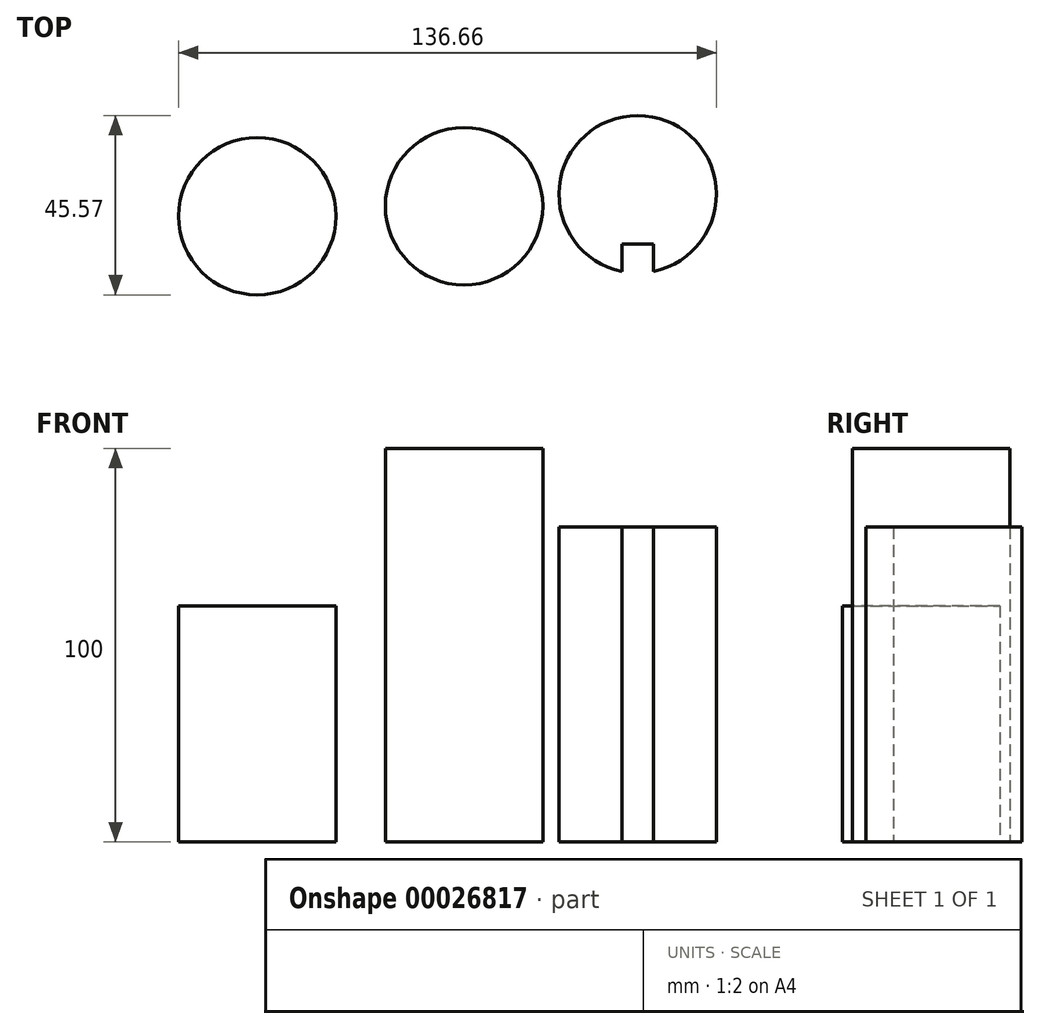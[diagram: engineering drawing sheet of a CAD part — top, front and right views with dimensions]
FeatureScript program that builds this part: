
annotation { "Feature Type Name" : "Feature", "Feature Type Description" : "" }
export const myFeature = defineFeature(function(context is Context, id is Id, definition is map)
    precondition{}
    {
        {
            var Q0;
            Q0=qCreatedBy(makeId("Top.planeOp"),FACE);
            var sketch = newSketch(context, id + "F0", { "sketchPlane" : qUnion([Q0])});
            skCircle(sketch, "E0", {"center": v(-42.04, 16.34) * mm, "radius": 20 * mm});
            skCircle(sketch, "E1", {"center": v(10.5, 18.86) * mm, "radius": 20 * mm});
            skCircle(sketch, "E2", {"center": v(54.62, 21.91) * mm, "radius": 20 * mm});
            skLineSegment(sketch, "E3", {"start": v(50.62, 2.32) * mm, "end": v(50.62, 9.32) * mm});
            skLineSegment(sketch, "E4", {"start": v(50.62, 9.32) * mm, "end": v(58.62, 9.32) * mm});
            skLineSegment(sketch, "E5", {"start": v(58.62, 9.32) * mm, "end": v(58.62, 2.32) * mm});
            skSolve(sketch);
        }
        {
            var Q0;
            Q0=makeQuery(id+"F0.imprint","IMPRINT",FACE,{"disambiguationData":[TD([[makeQuery(id+"F0.imprint","IMPRINT",EDGE,{"derivedFrom":sQuery(id+"F0.wireOp",EDGE,"E0")}),1.0]])]});
            extrude(context, id + "F1", {"entities" : qUnion([Q0]), "depth" : 60 * mm});
        }
        {
            var Q0;
            Q0=makeQuery(id+"F0.imprint","IMPRINT",FACE,{"disambiguationData":[TD([[makeQuery(id+"F0.imprint","IMPRINT",EDGE,{"derivedFrom":sQuery(id+"F0.wireOp",EDGE,"E1")}),1.0]])]});
            extrude(context, id + "F2", {"entities" : qUnion([Q0]), "depth" : 100 * mm});
        }
        {
            var Q0;
            {var subQ1=sQuery(id+"F0.wireOp",EDGE,"E3");Q0=makeQuery(id+"F0.imprint","IMPRINT",FACE,{"disambiguationData":[TD([[makeQuery(id+"F0.imprint","IMPRINT",EDGE,{"derivedFrom":subQ1}),1.0]])]});}
            extrude(context, id + "F3", {"entities" : qUnion([Q0]), "depth" : 80 * mm});
        }
    });
